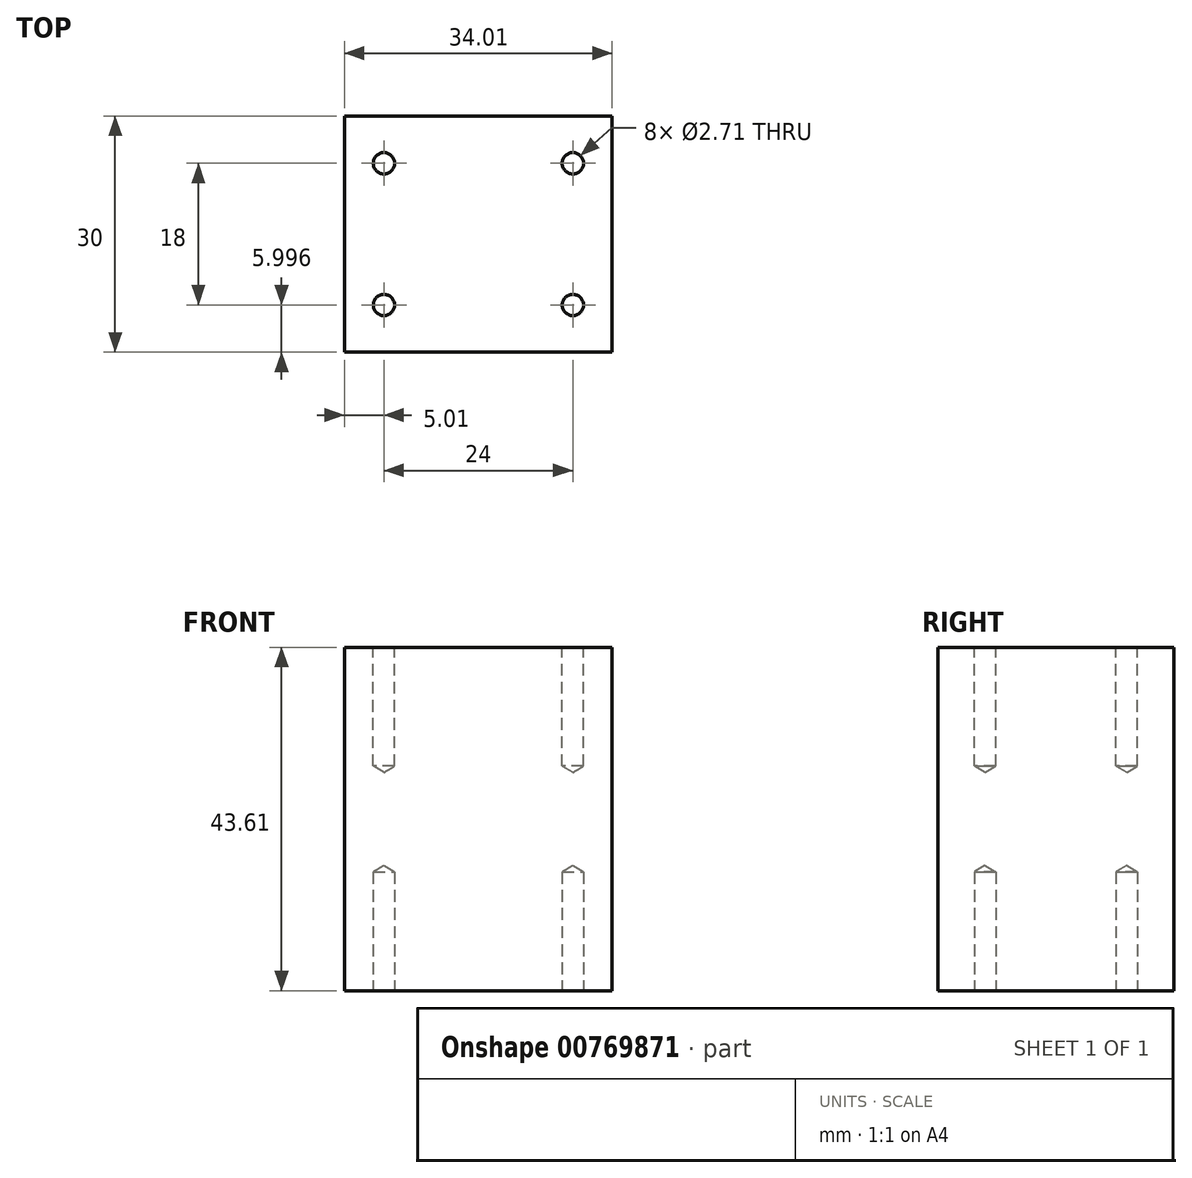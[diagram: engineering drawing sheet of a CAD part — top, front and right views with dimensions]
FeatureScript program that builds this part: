
annotation { "Feature Type Name" : "Feature", "Feature Type Description" : "" }
export const myFeature = defineFeature(function(context is Context, id is Id, definition is map)
    precondition{}
    {
        {
            var Q0;
            Q0=qCreatedBy(makeId("Top.planeOp"),FACE);
            var sketch = newSketch(context, id + "F0", { "sketchPlane" : qUnion([Q0])});
            skLineSegment(sketch, "E0.bottom", {"start": v(-15.3, 11.27) * mm, "end": v(18.72, 11.27) * mm});
            skLineSegment(sketch, "E0.top", {"start": v(-15.3, -18.73) * mm, "end": v(18.72, -18.73) * mm});
            skLineSegment(sketch, "E0.left", {"start": v(-15.3, 11.27) * mm, "end": v(-15.3, -18.73) * mm});
            skLineSegment(sketch, "E0.right", {"start": v(18.72, 11.27) * mm, "end": v(18.72, -18.73) * mm});
            skSolve(sketch);
        }
        {
            var Q0;
            Q0 = qSketchRegion(id + "F0", true);
            extrude(context, id + "F1", {"entities" : qUnion([Q0]), "oppositeDirection" : true, "depth" : 43.6 * mm, "offsetDistance" : 25.4 * mm});
        }
        {
            var Q0;
            Q0=makeQuery(id+"F1.opExtrude","CAP_FACE",FACE,{"disambiguationData":[OSD([sQuery(id+"F0.wireOp",EDGE,"E0.bottom"),sQuery(id+"F0.wireOp",EDGE,"E0.top"),sQuery(id+"F0.wireOp",EDGE,"E0.left"),sQuery(id+"F0.wireOp",EDGE,"E0.right")])],"isStart":true});
            var sketch = newSketch(context, id + "F2", { "sketchPlane" : qUnion([Q0])});
            skLineSegment(sketch, "E1", {"start": v(-10.28, 11.27) * mm, "end": v(-10.28, -18.73) * mm, "construction": true});
            skLineSegment(sketch, "E2", {"start": v(13.72, 11.27) * mm, "end": v(13.72, -18.73) * mm, "construction": true});
            skLineSegment(sketch, "E3", {"start": v(-10.28, -12.73) * mm, "end": v(13.72, -12.73) * mm, "construction": true});
            skLineSegment(sketch, "E4", {"start": v(-10.28, 5.27) * mm, "end": v(13.72, 5.27) * mm, "construction": true});
            skSolve(sketch);
        }
        {
            var Q0;
            Q0=makeQuery(id+"F1.opExtrude","CAP_FACE",FACE,{"disambiguationData":[OSD([sQuery(id+"F0.wireOp",EDGE,"E0.bottom"),sQuery(id+"F0.wireOp",EDGE,"E0.top"),sQuery(id+"F0.wireOp",EDGE,"E0.left"),sQuery(id+"F0.wireOp",EDGE,"E0.right")])],"isStart":false});
            var sketch = newSketch(context, id + "F3", { "sketchPlane" : qUnion([Q0])});
            skLineSegment(sketch, "E5.bottom", {"start": v(-10.28, 12.73) * mm, "end": v(13.72, 12.73) * mm, "construction": true});
            skLineSegment(sketch, "E5.top", {"start": v(-10.28, -5.27) * mm, "end": v(13.72, -5.27) * mm, "construction": true});
            skLineSegment(sketch, "E5.left", {"start": v(-10.28, 12.73) * mm, "end": v(-10.28, -5.27) * mm, "construction": true});
            skLineSegment(sketch, "E5.right", {"start": v(13.72, 12.73) * mm, "end": v(13.72, -5.27) * mm, "construction": true});
            skSolve(sketch);
        }
        {
            var Q0;
            Q0=sQuery(id+"F3.wireOp",VERTEX,"E5.bottom.start");
            var Q1;
            Q1=sQuery(id+"F3.wireOp",VERTEX,"E5.bottom.end");
            var Q2;
            Q2=sQuery(id+"F3.wireOp",VERTEX,"E5.top.end");
            var Q3;
            Q3=sQuery(id+"F3.wireOp",VERTEX,"E5.top.start");
            var Q4;
            Q4=sQuery(id+"F2.wireOp",VERTEX,"E4.start");
            var Q5;
            Q5=sQuery(id+"F2.wireOp",VERTEX,"E4.end");
            var Q6;
            Q6=sQuery(id+"F2.wireOp",VERTEX,"E3.end");
            var Q7;
            Q7=sQuery(id+"F2.wireOp",VERTEX,"E3.start");
            var Q8;
            Q8=makeQuery(id+"F1.opExtrude","SWEPT_BODY",BODY,{"disambiguationData":[OSD([sQuery(id+"F0.wireOp",EDGE,"E0.bottom"),sQuery(id+"F0.wireOp",EDGE,"E0.top"),sQuery(id+"F0.wireOp",EDGE,"E0.left"),sQuery(id+"F0.wireOp",EDGE,"E0.right")])]});
            hole(context, id + "F4", {"style" : HoleStyle.SIMPLE, "endStyle" : HoleEndStyle.BLIND, "standardTappedOrClearance" : lookupTablePath({ "standard" : "ANSI", "engagement" : "75%", "pitch" : "32 tpi", "size" : "#6", "type" : "Tapped" }), "standardBlindInLast" : lookupTablePath({ "standard" : "ANSI", "engagement" : "75%", "pitch" : "32 tpi", "size" : "#6", "type" : "Tapped" }), "holeDiameter" : 2.7 * mm, "majorDiameter" : 3.5 * mm, "showTappedDepth" : true, "holeDepth" : 15.1 * mm, "tappedDepth" : 12.7 * mm, "tapClearance" : 3, "locations" : qUnion([Q0, Q1, Q2, Q3, Q4, Q5, Q6, Q7]), "scope" : qUnion([Q8])});
        }
    });
